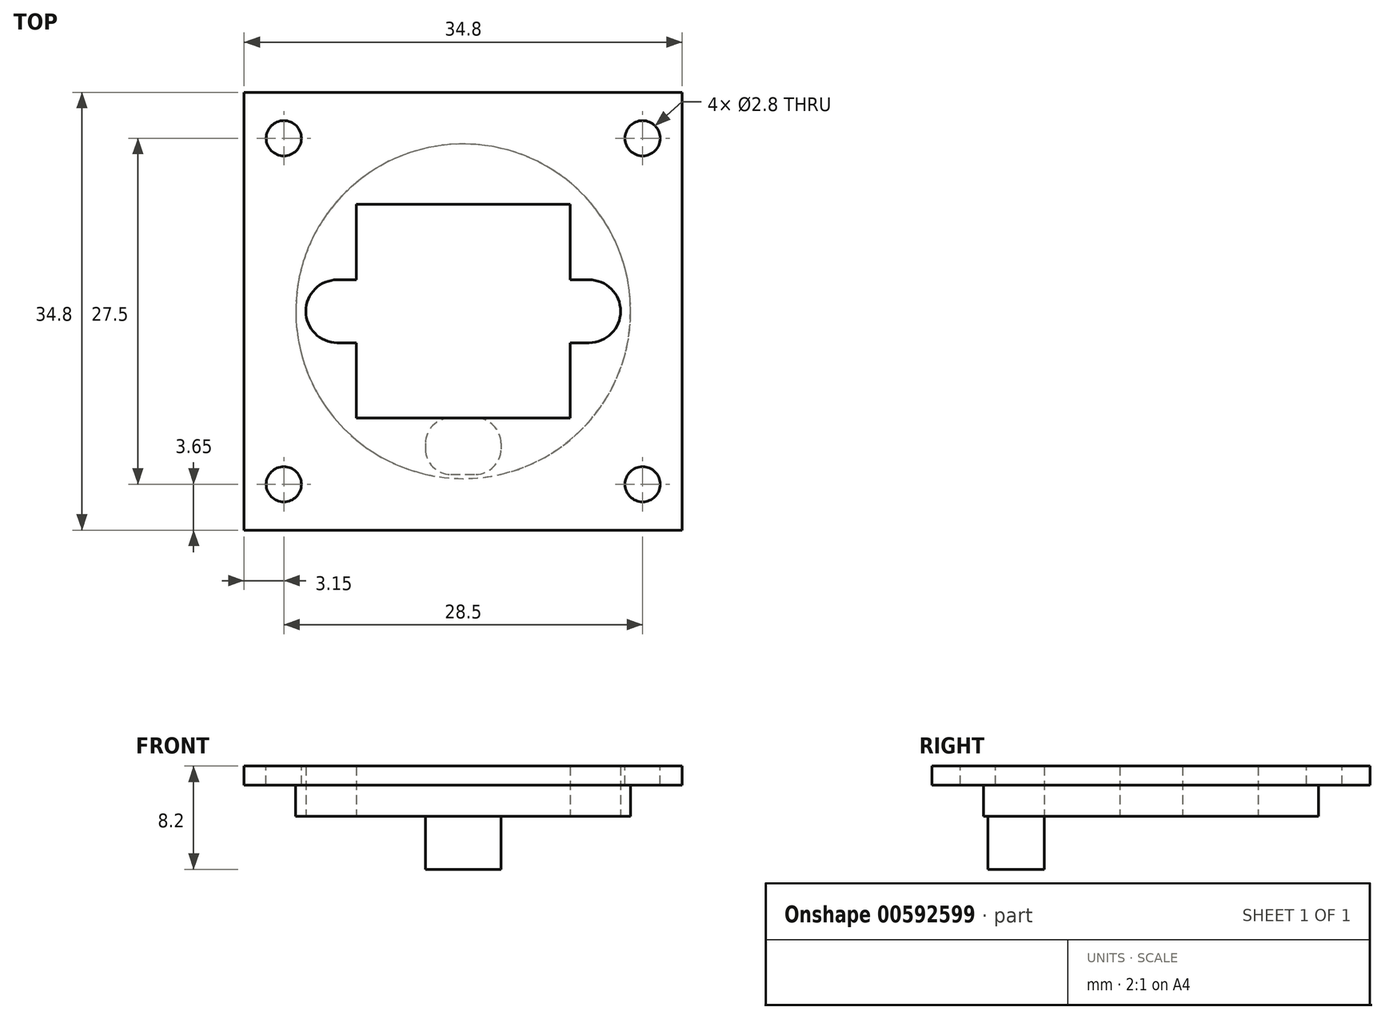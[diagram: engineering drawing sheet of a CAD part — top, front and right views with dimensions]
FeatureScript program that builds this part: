
annotation { "Feature Type Name" : "Feature", "Feature Type Description" : "" }
export const myFeature = defineFeature(function(context is Context, id is Id, definition is map)
    precondition{}
    {
        {
            var Q0;
            Q0=qCreatedBy(makeId("Top.planeOp"),FACE);
            var sketch = newSketch(context, id + "F0", { "sketchPlane" : qUnion([Q0])});
            skCircle(sketch, "E0", {"center": v(0, 0) * mm, "radius": 13.3 * mm});
            skLineSegment(sketch, "E1.bottom", {"start": v(-8.5, -8.5) * mm, "end": v(8.5, -8.5) * mm});
            skLineSegment(sketch, "E1.top", {"start": v(-8.5, 8.5) * mm, "end": v(8.5, 8.5) * mm});
            skLineSegment(sketch, "E1.left", {"start": v(-8.5, -8.5) * mm, "end": v(-8.5, 8.5) * mm});
            skLineSegment(sketch, "E1.right", {"start": v(8.5, -8.5) * mm, "end": v(8.5, 8.5) * mm});
            skLineSegment(sketch, "E2", {"start": v(0, -8.5) * mm, "end": v(0, 8.5) * mm});
            skCircle(sketch, "E3", {"center": v(10, 0) * mm, "radius": 2.5 * mm});
            skPoint(sketch, "E3.centerSnap0", {"position": v(8.5, 0) * mm});
            skLineSegment(sketch, "E4", {"start": v(8.5, 2.5) * mm, "end": v(10, 2.5) * mm});
            skLineSegment(sketch, "E5", {"start": v(8.5, -2.5) * mm, "end": v(10, -2.5) * mm});
            skCircle(sketch, "E6", {"center": v(-10, 0) * mm, "radius": 2.5 * mm});
            skPoint(sketch, "E6.centerSnap0", {"position": v(-8.5, 0) * mm});
            skLineSegment(sketch, "E7", {"start": v(-10, 2.5) * mm, "end": v(-8.5, 2.5) * mm});
            skLineSegment(sketch, "E8", {"start": v(-10, -2.5) * mm, "end": v(-8.5, -2.5) * mm});
            skSolve(sketch);
        }
        {
            var Q0;
            Q0=makeQuery(id+"F0.imprint","IMPRINT",FACE,{"disambiguationData":[TD([[makeQuery(id+"F0.imprint","IMPRINT",EDGE,{"derivedFrom":sQuery(id+"F0.wireOp",EDGE,"E0")}),1.0]])]});
            extrude(context, id + "F1", {"entities" : qUnion([Q0]), "depth" : 4 * mm, "offsetDistance" : 25 * mm});
        }
        {
            var Q0;
            Q0=makeQuery(id+"F1.opExtrude","CAP_FACE",FACE,{"disambiguationData":[OSD([sQuery(id+"F0.wireOp",EDGE,"E0"),sQuery(id+"F0.wireOp",EDGE,"E1.bottom"),sQuery(id+"F0.wireOp",EDGE,"E1.top"),sQuery(id+"F0.wireOp",EDGE,"E1.left"),sQuery(id+"F0.wireOp",EDGE,"E1.right"),sQuery(id+"F0.wireOp",EDGE,"E3"),sQuery(id+"F0.wireOp",EDGE,"E4"),sQuery(id+"F0.wireOp",EDGE,"E5"),sQuery(id+"F0.wireOp",EDGE,"E6"),sQuery(id+"F0.wireOp",EDGE,"E7"),sQuery(id+"F0.wireOp",EDGE,"E8")])],"isStart":true});
            var sketch = newSketch(context, id + "F2", { "sketchPlane" : qUnion([Q0])});
            skCircle(sketch, "E9.0.0", {"center": v(0, 0) * mm, "radius": 13.3 * mm});
            skLineSegment(sketch, "E10.0", {"start": v(-8.5, 8.5) * mm, "end": v(8.5, 8.5) * mm});
            skLineSegment(sketch, "E11", {"start": v(3, 8.5) * mm, "end": v(3, 12.96) * mm});
            skLineSegment(sketch, "E12", {"start": v(-3, 8.5) * mm, "end": v(-3, 12.96) * mm});
            skLineSegment(sketch, "E13", {"start": v(0, 8.5) * mm, "end": v(0, 13.3) * mm, "construction": true});
            skLineSegment(sketch, "E14", {"start": v(-3, 12.96) * mm, "end": v(3, 12.96) * mm});
            skSolve(sketch);
        }
        {
            var Q0;
            {var subQ0=sQuery(id+"F2.wireOp",EDGE,"E11");Q0=makeQuery(id+"F2.imprint","IMPRINT",FACE,{"disambiguationData":[TD([[makeQuery(id+"F2.imprint","IMPRINT",EDGE,{"derivedFrom":subQ0}),1.0]])]});}
            extrude(context, id + "F3", {"entities" : qUnion([Q0]), "operationType" : NewBodyOperationType.ADD, "depth" : 4.2 * mm, "offsetDistance" : 25 * mm});
        }
        {
            var Q0;
            Q0=makeQuery(id+"F3.opExtrude","SWEPT_EDGE",EDGE,{"disambiguationData":[OSD([sQuery(id+"F2.wireOp",EDGE,"E9.0.0"),sQuery(id+"F2.wireOp",EDGE,"E12"),sQuery(id+"F2.wireOp",EDGE,"E14")])]});
            var Q1;
            Q1=makeQuery(id+"F3.opExtrude","SWEPT_EDGE",EDGE,{"disambiguationData":[OSD([sQuery(id+"F2.wireOp",EDGE,"E10.0"),sQuery(id+"F2.wireOp",EDGE,"E12")])]});
            var Q2;
            Q2=makeQuery(id+"F3.opExtrude","SWEPT_EDGE",EDGE,{"disambiguationData":[OSD([sQuery(id+"F2.wireOp",EDGE,"E10.0"),sQuery(id+"F2.wireOp",EDGE,"E11")])]});
            var Q3;
            Q3=makeQuery(id+"F3.opExtrude","SWEPT_EDGE",EDGE,{"disambiguationData":[OSD([sQuery(id+"F2.wireOp",EDGE,"E9.0.0"),sQuery(id+"F2.wireOp",EDGE,"E11"),sQuery(id+"F2.wireOp",EDGE,"E14")])]});
            fillet(context, id + "F4", {"entities" : qUnion([Q0, Q1, Q2, Q3]), "radius" : 2 * mm, "tangentPropagation" : true, "allowEdgeOverflow" : false});
        }
        {
            var Q0;
            Q0=makeQuery(id+"F1.opExtrude","CAP_FACE",FACE,{"disambiguationData":[OSD([sQuery(id+"F0.wireOp",EDGE,"E0"),sQuery(id+"F0.wireOp",EDGE,"E1.bottom"),sQuery(id+"F0.wireOp",EDGE,"E1.top"),sQuery(id+"F0.wireOp",EDGE,"E1.left"),sQuery(id+"F0.wireOp",EDGE,"E1.right"),sQuery(id+"F0.wireOp",EDGE,"E3"),sQuery(id+"F0.wireOp",EDGE,"E4"),sQuery(id+"F0.wireOp",EDGE,"E5"),sQuery(id+"F0.wireOp",EDGE,"E6"),sQuery(id+"F0.wireOp",EDGE,"E7"),sQuery(id+"F0.wireOp",EDGE,"E8")])],"isStart":false});
            var sketch = newSketch(context, id + "F5", { "sketchPlane" : qUnion([Q0])});
            skCircle(sketch, "E15.0", {"center": v(0, 0) * mm, "radius": 13.3 * mm});
            skLineSegment(sketch, "E16.bottom", {"start": v(-17.4, 17.4) * mm, "end": v(17.4, 17.4) * mm});
            skLineSegment(sketch, "E16.top", {"start": v(-17.4, -17.4) * mm, "end": v(17.4, -17.4) * mm});
            skLineSegment(sketch, "E16.left", {"start": v(-17.4, 17.4) * mm, "end": v(-17.4, -17.4) * mm});
            skLineSegment(sketch, "E16.right", {"start": v(17.4, 17.4) * mm, "end": v(17.4, -17.4) * mm});
            skLineSegment(sketch, "E17", {"start": v(0, 17.4) * mm, "end": v(0, -17.4) * mm});
            skLineSegment(sketch, "E18", {"start": v(0, 0) * mm, "end": v(17.4, 4.5) * mm, "construction": true});
            skCircle(sketch, "E19", {"center": v(-14.25, -13.75) * mm, "radius": 1.4 * mm});
            skCircle(sketch, "E20", {"center": v(14.25, -13.75) * mm, "radius": 1.4 * mm});
            skLineSegment(sketch, "E21", {"start": v(-14.25, -13.75) * mm, "end": v(14.25, -13.75) * mm});
            skLineSegment(sketch, "E22", {"start": v(0, -13.75) * mm, "end": v(0, 0) * mm, "construction": true});
            skCircle(sketch, "E23", {"center": v(-14.25, 13.75) * mm, "radius": 1.4 * mm});
            skCircle(sketch, "E24", {"center": v(14.25, 13.75) * mm, "radius": 1.4 * mm});
            skLineSegment(sketch, "E25", {"start": v(-14.25, 13.75) * mm, "end": v(-14.25, -13.75) * mm});
            skLineSegment(sketch, "E26", {"start": v(-14.25, 0) * mm, "end": v(0, 0) * mm});
            skSolve(sketch);
        }
        {
            var Q0;
            Q0 = qSketchRegion(id + "F5", true);
            var Q1;
            {var subQ5=sQuery(id+"F5.wireOp",EDGE,"E15.0");var subQ7=sQuery(id+"F5.wireOp",EDGE,"E26");var subQ10=makeQuery(id+"F5.imprint","INTERSECT",VERTEX,{"derivedFrom":[subQ5,subQ7]});Q1=makeQuery(id+"F5.imprint","IMPRINT",FACE,{"disambiguationData":[TD([[makeQuery(id+"F5.imprint","IMPRINT",EDGE,{"disambiguationData":[TD([[subQ10,-1.0]])],"derivedFrom":subQ5}),-1.0]])]});}
            var Q2;
            {var subQ2=sQuery(id+"F0.wireOp",EDGE,"E8");var subQ13=makeQuery(id+"F1.opExtrude","CAP_EDGE",EDGE,{"disambiguationData":[OSD([subQ2])],"isStart":false});Q2=makeQuery(id+"F5.imprint","IMPRINT",FACE,{"disambiguationData":[TD([[makeQuery(id+"F5.imprint","IMPRINT",EDGE,{"derivedFrom":subQ13}),-1.0]])]});}
            var Q3;
            Q3=makeQuery(id+"F5.imprint","IMPRINT",FACE,{"disambiguationData":[TD([[makeQuery(id+"F5.imprint","IMPRINT",EDGE,{"derivedFrom":makeQuery(id+"F1.opExtrude","CAP_EDGE",EDGE,{"disambiguationData":[OSD([sQuery(id+"F0.wireOp",EDGE,"E3")])],"isStart":false})}),-1.0]])]});
            var Q4;
            {var subQ2=sQuery(id+"F0.wireOp",EDGE,"E7");var subQ13=makeQuery(id+"F1.opExtrude","CAP_EDGE",EDGE,{"disambiguationData":[OSD([subQ2])],"isStart":false});Q4=makeQuery(id+"F5.imprint","IMPRINT",FACE,{"disambiguationData":[TD([[makeQuery(id+"F5.imprint","IMPRINT",EDGE,{"derivedFrom":subQ13}),1.0]])]});}
            extrude(context, id + "F6", {"entities" : qUnion([Q0, Q1, Q2, Q3, Q4]), "operationType" : NewBodyOperationType.ADD, "oppositeDirection" : true, "depth" : 1.5 * mm, "offsetDistance" : 25 * mm});
        }
    });
